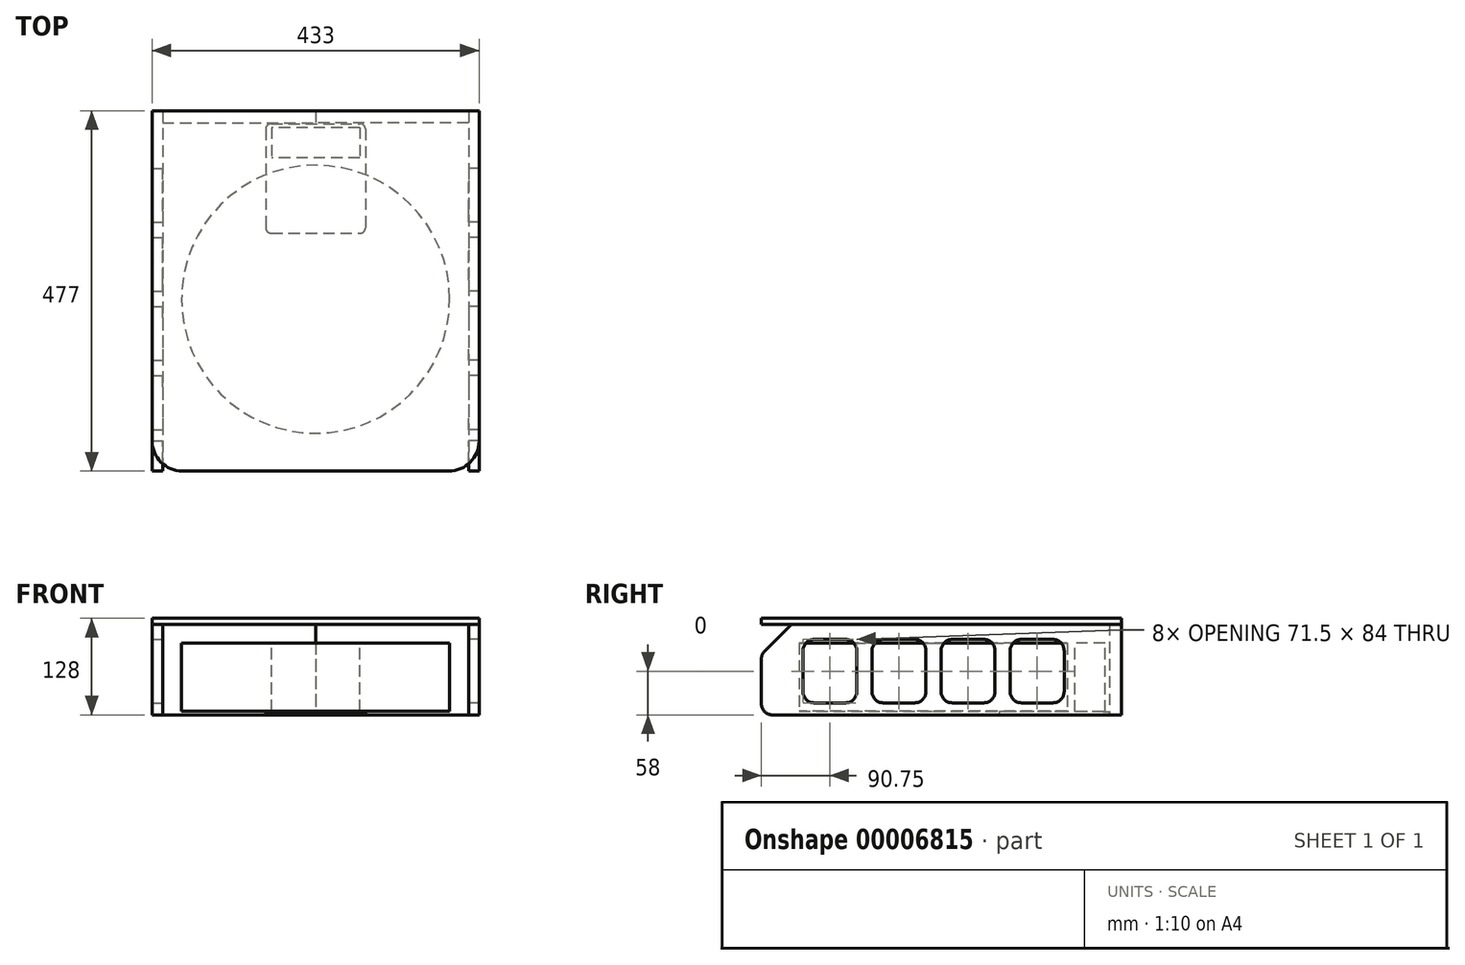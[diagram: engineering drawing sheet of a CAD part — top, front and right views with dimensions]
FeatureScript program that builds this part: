
annotation { "Feature Type Name" : "Feature", "Feature Type Description" : "" }
export const myFeature = defineFeature(function(context is Context, id is Id, definition is map)
    precondition{}
    {
        {
            var Q0;
            Q0=qCreatedBy(makeId("Front.planeOp"),FACE);
            var sketch = newSketch(context, id + "F0", { "sketchPlane" : qUnion([Q0])});
            skLineSegment(sketch, "E0", {"start": v(0, 0) * mm, "end": v(0, 117.94) * mm, "construction": true});
            skPoint(sketch, "E1", {"position": v(0, 5) * mm});
            skPoint(sketch, "E2", {"position": v(0, 95) * mm});
            skSolve(sketch);
        }
        {
            var Q0;
            Q0=qCreatedBy(makeId("Top.planeOp"),FACE);
            var Q1;
            Q1=sQuery(id+"F0.wireOp",VERTEX,"E1");
            cPlane(context, id + "F1", {"entities" : qUnion([Q0, Q1]), "cplaneType" : CPlaneType.PLANE_POINT, "offset" : 25 * mm, "width" : 150 * mm, "height" : 150 * mm});
        }
        {
            var Q0;
            Q0=qCreatedBy(id+"F1.planeOp",FACE);
            var sketch = newSketch(context, id + "F2", { "sketchPlane" : qUnion([Q0])});
            skCircle(sketch, "E3", {"center": v(0, 0) * mm, "radius": 177.5 * mm});
            skSolve(sketch);
        }
        {
            var Q0;
            Q0 = qSketchRegion(id + "F2", true);
            extrude(context, id + "F3", {"entities" : qUnion([Q0]), "depth" : 90 * mm});
        }
        {
            var Q0;
            Q0=qCreatedBy(id+"F1.planeOp",FACE);
            var sketch = newSketch(context, id + "F4", { "sketchPlane" : qUnion([Q0])});
            skLineSegment(sketch, "E4.bottom", {"start": v(-58.5, 227.5) * mm, "end": v(58.5, 227.5) * mm});
            skLineSegment(sketch, "E4.top", {"start": v(-58.5, 187.5) * mm, "end": v(58.5, 187.5) * mm});
            skLineSegment(sketch, "E4.left", {"start": v(-58.5, 187.5) * mm, "end": v(-58.5, 227.5) * mm});
            skLineSegment(sketch, "E4.right", {"start": v(58.5, 187.5) * mm, "end": v(58.5, 227.5) * mm});
            skLineSegment(sketch, "E5", {"start": v(0, 0) * mm, "end": v(0, 187.5) * mm, "construction": true});
            skSolve(sketch);
        }
        {
            var Q0;
            Q0 = qSketchRegion(id + "F4", true);
            var Q1;
            Q1=qCreatedBy(makeId("Top.planeOp"),FACE);
            var Q2;
            Q2=makeQuery(id+"F3.opExtrude","CAP_FACE",FACE,{"disambiguationData":[OSD([sQuery(id+"F2.wireOp",EDGE,"E3")])],"isStart":false});
            extrude(context, id + "F5", {"entities" : qUnion([Q0]), "endBound" : BoundingType.UP_TO_SURFACE, "oppositeDirection" : true, "endBoundEntityFace" : qUnion([Q1]), "depth" : 100 * mm, "hasSecondDirection" : true, "secondDirectionBound" : SecondDirectionBoundingType.UP_TO_SURFACE, "secondDirectionOppositeDirection" : false, "secondDirectionBoundEntityFace" : qUnion([Q2]), "secondDirectionDepth" : 25 * mm});
        }
        {
            var Q0;
            Q0=qCreatedBy(makeId("Top.planeOp"),FACE);
            var sketch = newSketch(context, id + "F6", { "sketchPlane" : qUnion([Q0])});
            skLineSegment(sketch, "E6.bottom", {"start": v(-59, 232.5) * mm, "end": v(59, 232.5) * mm});
            skLineSegment(sketch, "E6.top", {"start": v(-59, 87.5) * mm, "end": v(59, 87.5) * mm});
            skLineSegment(sketch, "E6.left", {"start": v(-66, 225.5) * mm, "end": v(-66, 94.5) * mm});
            skLineSegment(sketch, "E6.right", {"start": v(66, 225.5) * mm, "end": v(66, 94.5) * mm});
            skPoint(sketch, "E7.visualSharp", {"position": v(-66, 232.5) * mm});
            skArc(sketch, "E7.filletArc", {"start": v(-59, 232.5) * mm, "mid": v(-63.95, 230.45) * mm, "end": v(-66, 225.5) * mm});
            skPoint(sketch, "E8.visualSharp", {"position": v(66, 232.5) * mm});
            skArc(sketch, "E8.filletArc", {"start": v(66, 225.5) * mm, "mid": v(63.95, 230.45) * mm, "end": v(59, 232.5) * mm});
            skPoint(sketch, "E9.visualSharp", {"position": v(66, 87.5) * mm});
            skArc(sketch, "E9.filletArc", {"start": v(59, 87.5) * mm, "mid": v(63.95, 89.55) * mm, "end": v(66, 94.5) * mm});
            skPoint(sketch, "E10.visualSharp", {"position": v(-66, 87.5) * mm});
            skArc(sketch, "E10.filletArc", {"start": v(-66, 94.5) * mm, "mid": v(-63.95, 89.55) * mm, "end": v(-59, 87.5) * mm});
            skLineSegment(sketch, "E11", {"start": v(0, 0) * mm, "end": v(0, 87.5) * mm, "construction": true});
            skSolve(sketch);
        }
        {
            var Q0;
            Q0 = qSketchRegion(id + "F6", true);
            extrude(context, id + "F7", {"entities" : qUnion([Q0]), "operationType" : NewBodyOperationType.ADD, "depth" : 4.5 * mm});
        }
        {
            var Q0;
            Q0=makeQuery(id+"F2.imprint","IMPRINT",FACE,{"disambiguationData":[TD([[makeQuery(id+"F2.imprint","IMPRINT",EDGE,{"derivedFrom":sQuery(id+"F2.wireOp",EDGE,"E3")}),1.0]])]});
            var sketch = newSketch(context, id + "F8", { "sketchPlane" : qUnion([Q0])});
            skLineSegment(sketch, "E12", {"start": v(0, -177.5) * mm, "end": v(0, 233.5) * mm, "construction": true});
            skLineSegment(sketch, "E13", {"start": v(-177.5, 233.5) * mm, "end": v(0, 233.5) * mm, "construction": true});
            skLineSegment(sketch, "E14", {"start": v(-177.5, 233.5) * mm, "end": v(-177.5, -177.5) * mm, "construction": true});
            skLineSegment(sketch, "E15", {"start": v(0, -177.5) * mm, "end": v(-177.5, -177.5) * mm, "construction": true});
            skSolve(sketch);
        }
        {
            var Q0;
            Q0=qCreatedBy(makeId("Front.planeOp"),FACE);
            var Q1;
            Q1=sQuery(id+"F8.wireOp",VERTEX,"E12.end");
            cPlane(context, id + "F9", {"entities" : qUnion([Q0, Q1]), "cplaneType" : CPlaneType.PLANE_POINT, "offset" : 25 * mm, "width" : 150 * mm, "height" : 150 * mm});
        }
        {
            var Q0;
            Q0=qCreatedBy(id+"F9.planeOp",FACE);
            var sketch = newSketch(context, id + "F10", { "sketchPlane" : qUnion([Q0])});
            skLineSegment(sketch, "E16.bottom", {"start": v(-202.5, 120) * mm, "end": v(0, 120) * mm});
            skLineSegment(sketch, "E16.top", {"start": v(-202.5, 0) * mm, "end": v(0, 0) * mm});
            skLineSegment(sketch, "E16.left", {"start": v(-202.5, 120) * mm, "end": v(-202.5, 0) * mm});
            skLineSegment(sketch, "E16.right", {"start": v(0, 120) * mm, "end": v(0, 0) * mm});
            skLineSegment(sketch, "E17", {"start": v(-156.5, 114) * mm, "end": v(-200.5, 114) * mm, "construction": true});
            skLineSegment(sketch, "E18", {"start": v(-200.5, 114) * mm, "end": v(-200.5, 76.5) * mm, "construction": true});
            skLineSegment(sketch, "E19", {"start": v(-156.5, 76.5) * mm, "end": v(-156.5, 114) * mm, "construction": true});
            skLineSegment(sketch, "E20", {"start": v(-156.5, 76.5) * mm, "end": v(-200.5, 76.5) * mm, "construction": true});
            skLineSegment(sketch, "E21", {"start": v(-156.5, 90) * mm, "end": v(-162.5, 90) * mm, "construction": true});
            skLineSegment(sketch, "E22", {"start": v(-162.5, 90) * mm, "end": v(-194.5, 90) * mm, "construction": true});
            skLineSegment(sketch, "E23", {"start": v(-194.5, 90) * mm, "end": v(-200.5, 90) * mm, "construction": true});
            skLineSegment(sketch, "E24", {"start": v(-156.5, 108) * mm, "end": v(-162.5, 108) * mm, "construction": true});
            skLineSegment(sketch, "E25", {"start": v(-162.5, 108) * mm, "end": v(-194.5, 108) * mm, "construction": true});
            skLineSegment(sketch, "E26", {"start": v(-194.5, 108) * mm, "end": v(-200.5, 108) * mm, "construction": true});
            skCircle(sketch, "E27", {"center": v(-162.5, 108) * mm, "radius": 2 * mm, "construction": true});
            skCircle(sketch, "E28", {"center": v(-194.5, 108) * mm, "radius": 2 * mm, "construction": true});
            skCircle(sketch, "E29", {"center": v(-194.5, 90) * mm, "radius": 2 * mm, "construction": true});
            skCircle(sketch, "E30", {"center": v(-162.5, 90) * mm, "radius": 2 * mm, "construction": true});
            skLineSegment(sketch, "E31", {"start": v(-162.5, 90) * mm, "end": v(-194.5, 108) * mm, "construction": true});
            skLineSegment(sketch, "E32", {"start": v(-162.5, 108) * mm, "end": v(-194.5, 90) * mm, "construction": true});
            skPoint(sketch, "E33", {"position": v(-178.5, 99) * mm});
            skSolve(sketch);
        }
        {
            var Q0;
            Q0 = qSketchRegion(id + "F10", true);
            extrude(context, id + "F11", {"entities" : qUnion([Q0]), "oppositeDirection" : true, "depth" : 16 * mm});
        }
        {
            var Q0;
            Q0=qCreatedBy(makeId("Front.planeOp"),FACE);
            var Q1;
            Q1=sQuery(id+"F8.wireOp",VERTEX,"E15.start");
            cPlane(context, id + "F12", {"entities" : qUnion([Q0, Q1]), "cplaneType" : CPlaneType.PLANE_POINT, "offset" : 25 * mm, "width" : 150 * mm, "height" : 150 * mm});
        }
        {
            var Q0;
            Q0=makeQuery(id+"F11.opExtrude","SWEPT_FACE",FACE,{"disambiguationData":[OSD([sQuery(id+"F10.wireOp",EDGE,"E16.left")])]});
            var sketch = newSketch(context, id + "F13", { "sketchPlane" : qUnion([Q0])});
            skLineSegment(sketch, "E34", {"start": v(-249.5, 120) * mm, "end": v(-249.5, 0) * mm});
            skLineSegment(sketch, "E35", {"start": v(227.5, 0) * mm, "end": v(-249.5, 0) * mm});
            skLineSegment(sketch, "E36", {"start": v(227.5, 0) * mm, "end": v(227.5, 80) * mm});
            skLineSegment(sketch, "E37", {"start": v(227.5, 80) * mm, "end": v(187.5, 120) * mm});
            skLineSegment(sketch, "E38", {"start": v(-249.5, 120) * mm, "end": v(187.5, 120) * mm});
            skLineSegment(sketch, "E39.bottom", {"start": v(-102, 100) * mm, "end": v(-173.5, 100) * mm});
            skLineSegment(sketch, "E39.top", {"start": v(-102, 16) * mm, "end": v(-173.5, 16) * mm});
            skLineSegment(sketch, "E39.left", {"start": v(-173.5, 100) * mm, "end": v(-173.5, 16) * mm});
            skLineSegment(sketch, "E39.right", {"start": v(-102, 100) * mm, "end": v(-102, 16) * mm});
            skLineSegment(sketch, "E40.bottom", {"start": v(-10.5, 100) * mm, "end": v(-82, 100) * mm});
            skLineSegment(sketch, "E40.left", {"start": v(-82, 100) * mm, "end": v(-82, 16) * mm});
            skLineSegment(sketch, "E41.top", {"start": v(-10.5, 16) * mm, "end": v(-82, 16) * mm});
            skLineSegment(sketch, "E41.left", {"start": v(-10.5, 100) * mm, "end": v(-10.5, 16) * mm});
            skLineSegment(sketch, "E42.bottom", {"start": v(101, 100) * mm, "end": v(172.5, 100) * mm});
            skLineSegment(sketch, "E42.top", {"start": v(101, 16) * mm, "end": v(172.5, 16) * mm});
            skLineSegment(sketch, "E42.left", {"start": v(101, 100) * mm, "end": v(101, 16) * mm});
            skLineSegment(sketch, "E42.right", {"start": v(172.5, 100) * mm, "end": v(172.5, 16) * mm});
            skLineSegment(sketch, "E43", {"start": v(227.5, 80) * mm, "end": v(227.5, 120) * mm, "construction": true});
            skLineSegment(sketch, "E44.bottom", {"start": v(9.5, 100) * mm, "end": v(81, 100) * mm});
            skLineSegment(sketch, "E44.top", {"start": v(9.5, 16) * mm, "end": v(81, 16) * mm});
            skLineSegment(sketch, "E44.left", {"start": v(81, 100) * mm, "end": v(81, 16) * mm});
            skLineSegment(sketch, "E44.right", {"start": v(9.5, 100) * mm, "end": v(9.5, 16) * mm});
            skPoint(sketch, "E45", {"position": v(101, 120) * mm});
            skLineSegment(sketch, "E46", {"start": v(187.5, 120) * mm, "end": v(187.5, 0) * mm, "construction": true});
            skLineSegment(sketch, "E47", {"start": v(-102, 16) * mm, "end": v(-82, 16) * mm, "construction": true});
            skLineSegment(sketch, "E48", {"start": v(9.5, 16) * mm, "end": v(-10.5, 16) * mm, "construction": true});
            skLineSegment(sketch, "E49", {"start": v(81, 16) * mm, "end": v(101, 16) * mm, "construction": true});
            skPoint(sketch, "E50", {"position": v(177.5, 23.11) * mm});
            skSolve(sketch);
        }
        {
            var Q0;
            Q0 = qSketchRegion(id + "F13", true);
            extrude(context, id + "F14", {"entities" : qUnion([Q0]), "depth" : 14 * mm});
        }
        {
            var Q0;
            Q0=makeQuery(id+"F14.opExtrude","SWEPT_FACE",FACE,{"disambiguationData":[OSD([sQuery(id+"F13.wireOp",EDGE,"E38")])]});
            var sketch = newSketch(context, id + "F15", { "sketchPlane" : qUnion([Q0])});
            skLineSegment(sketch, "E51", {"start": v(-216.5, -144.25) * mm, "end": v(-202.5, -144.25) * mm, "construction": true});
            skCircle(sketch, "E52", {"center": v(-209.5, -144.25) * mm, "radius": 5.05 * mm});
            skSolve(sketch);
        }
        {
            var Q0;
            Q0=makeQuery(id+"F14.opExtrude","SWEPT_EDGE",EDGE,{"disambiguationData":[OSD([sQuery(id+"F13.wireOp",EDGE,"E40.bottom"),sQuery(id+"F13.wireOp",EDGE,"E40.left")])]});
            var Q1;
            Q1=makeQuery(id+"F14.opExtrude","SWEPT_EDGE",EDGE,{"disambiguationData":[OSD([sQuery(id+"F13.wireOp",EDGE,"E39.bottom"),sQuery(id+"F13.wireOp",EDGE,"E39.left")])]});
            var Q2;
            Q2=makeQuery(id+"F14.opExtrude","SWEPT_EDGE",EDGE,{"disambiguationData":[OSD([sQuery(id+"F13.wireOp",EDGE,"E41.bottom"),sQuery(id+"F13.wireOp",EDGE,"E41.left")])]});
            var Q3;
            Q3=makeQuery(id+"F14.opExtrude","SWEPT_EDGE",EDGE,{"disambiguationData":[OSD([sQuery(id+"F13.wireOp",EDGE,"E35"),sQuery(id+"F13.wireOp",EDGE,"E36")])]});
            var Q4;
            Q4=makeQuery(id+"F14.opExtrude","SWEPT_EDGE",EDGE,{"disambiguationData":[OSD([sQuery(id+"F13.wireOp",EDGE,"E36"),sQuery(id+"F13.wireOp",EDGE,"E37")])]});
            var Q5;
            Q5=makeQuery(id+"F14.opExtrude","SWEPT_EDGE",EDGE,{"disambiguationData":[OSD([sQuery(id+"F13.wireOp",EDGE,"E39.top"),sQuery(id+"F13.wireOp",EDGE,"E39.left")])]});
            var Q6;
            Q6=makeQuery(id+"F14.opExtrude","SWEPT_EDGE",EDGE,{"disambiguationData":[OSD([sQuery(id+"F13.wireOp",EDGE,"E40.top"),sQuery(id+"F13.wireOp",EDGE,"E40.left")])]});
            var Q7;
            Q7=makeQuery(id+"F14.opExtrude","SWEPT_EDGE",EDGE,{"disambiguationData":[OSD([sQuery(id+"F13.wireOp",EDGE,"E41.top"),sQuery(id+"F13.wireOp",EDGE,"E41.left")])]});
            var Q8;
            Q8=makeQuery(id+"F14.opExtrude","SWEPT_EDGE",EDGE,{"disambiguationData":[OSD([sQuery(id+"F13.wireOp",EDGE,"E41.top"),sQuery(id+"F13.wireOp",EDGE,"E41.right")])]});
            var Q9;
            Q9=makeQuery(id+"F14.opExtrude","SWEPT_EDGE",EDGE,{"disambiguationData":[OSD([sQuery(id+"F13.wireOp",EDGE,"E40.top"),sQuery(id+"F13.wireOp",EDGE,"E40.right")])]});
            var Q10;
            Q10=makeQuery(id+"F14.opExtrude","SWEPT_EDGE",EDGE,{"disambiguationData":[OSD([sQuery(id+"F13.wireOp",EDGE,"E39.top"),sQuery(id+"F13.wireOp",EDGE,"E39.right")])]});
            var Q11;
            Q11=makeQuery(id+"F14.opExtrude","SWEPT_EDGE",EDGE,{"disambiguationData":[OSD([sQuery(id+"F13.wireOp",EDGE,"E41.bottom"),sQuery(id+"F13.wireOp",EDGE,"E41.right")])]});
            var Q12;
            Q12=makeQuery(id+"F14.opExtrude","SWEPT_EDGE",EDGE,{"disambiguationData":[OSD([sQuery(id+"F13.wireOp",EDGE,"E40.bottom"),sQuery(id+"F13.wireOp",EDGE,"E40.right")])]});
            var Q13;
            Q13=makeQuery(id+"F14.opExtrude","SWEPT_EDGE",EDGE,{"disambiguationData":[OSD([sQuery(id+"F13.wireOp",EDGE,"E39.bottom"),sQuery(id+"F13.wireOp",EDGE,"E39.right")])]});
            var Q14;
            Q14=makeQuery(id+"F14.opExtrude","SWEPT_EDGE",EDGE,{"disambiguationData":[OSD([sQuery(id+"F13.wireOp",EDGE,"E42.top"),sQuery(id+"F13.wireOp",EDGE,"E42.left")])]});
            var Q15;
            Q15=makeQuery(id+"F14.opExtrude","SWEPT_EDGE",EDGE,{"disambiguationData":[OSD([sQuery(id+"F13.wireOp",EDGE,"E42.top"),sQuery(id+"F13.wireOp",EDGE,"E42.right")])]});
            var Q16;
            Q16=makeQuery(id+"F14.opExtrude","SWEPT_EDGE",EDGE,{"disambiguationData":[OSD([sQuery(id+"F13.wireOp",EDGE,"E42.bottom"),sQuery(id+"F13.wireOp",EDGE,"E42.right")])]});
            var Q17;
            Q17=makeQuery(id+"F14.opExtrude","SWEPT_EDGE",EDGE,{"disambiguationData":[OSD([sQuery(id+"F13.wireOp",EDGE,"E42.bottom"),sQuery(id+"F13.wireOp",EDGE,"E42.left")])]});
            var Q18;
            Q18=makeQuery(id+"F11.opExtrude","SWEPT_EDGE",EDGE,{"disambiguationData":[OSD([sQuery(id+"F10.wireOp",EDGE,"42908f74-1b4f-4dd7-a1f5-b5feeaa3a12f.bottom"),sQuery(id+"F10.wireOp",EDGE,"42908f74-1b4f-4dd7-a1f5-b5feeaa3a12f.right")])]});
            var Q19;
            Q19=makeQuery(id+"F11.opExtrude","SWEPT_EDGE",EDGE,{"disambiguationData":[OSD([sQuery(id+"F10.wireOp",EDGE,"7d3d7e17-e7ec-4853-b92f-0c4755d0859e.bottom"),sQuery(id+"F10.wireOp",EDGE,"7d3d7e17-e7ec-4853-b92f-0c4755d0859e.right")])]});
            var Q20;
            Q20=makeQuery(id+"F11.opExtrude","SWEPT_EDGE",EDGE,{"disambiguationData":[OSD([sQuery(id+"F10.wireOp",EDGE,"7d3d7e17-e7ec-4853-b92f-0c4755d0859e.top"),sQuery(id+"F10.wireOp",EDGE,"7d3d7e17-e7ec-4853-b92f-0c4755d0859e.right")])]});
            var Q21;
            Q21=makeQuery(id+"F11.opExtrude","SWEPT_EDGE",EDGE,{"disambiguationData":[OSD([sQuery(id+"F10.wireOp",EDGE,"42908f74-1b4f-4dd7-a1f5-b5feeaa3a12f.top"),sQuery(id+"F10.wireOp",EDGE,"42908f74-1b4f-4dd7-a1f5-b5feeaa3a12f.right")])]});
            var Q22;
            Q22=makeQuery(id+"F11.opExtrude","SWEPT_EDGE",EDGE,{"disambiguationData":[OSD([sQuery(id+"F10.wireOp",EDGE,"7d3d7e17-e7ec-4853-b92f-0c4755d0859e.bottom"),sQuery(id+"F10.wireOp",EDGE,"7d3d7e17-e7ec-4853-b92f-0c4755d0859e.left")])]});
            var Q23;
            Q23=makeQuery(id+"F11.opExtrude","SWEPT_EDGE",EDGE,{"disambiguationData":[OSD([sQuery(id+"F10.wireOp",EDGE,"42908f74-1b4f-4dd7-a1f5-b5feeaa3a12f.bottom"),sQuery(id+"F10.wireOp",EDGE,"42908f74-1b4f-4dd7-a1f5-b5feeaa3a12f.left")])]});
            var Q24;
            Q24=makeQuery(id+"F11.opExtrude","SWEPT_EDGE",EDGE,{"disambiguationData":[OSD([sQuery(id+"F10.wireOp",EDGE,"42908f74-1b4f-4dd7-a1f5-b5feeaa3a12f.top"),sQuery(id+"F10.wireOp",EDGE,"42908f74-1b4f-4dd7-a1f5-b5feeaa3a12f.left")])]});
            var Q25;
            Q25=makeQuery(id+"F11.opExtrude","SWEPT_EDGE",EDGE,{"disambiguationData":[OSD([sQuery(id+"F10.wireOp",EDGE,"7d3d7e17-e7ec-4853-b92f-0c4755d0859e.top"),sQuery(id+"F10.wireOp",EDGE,"7d3d7e17-e7ec-4853-b92f-0c4755d0859e.left")])]});
            var Q26;
            Q26=makeQuery(id+"F14.opExtrude","SWEPT_EDGE",EDGE,{"disambiguationData":[OSD([sQuery(id+"F13.wireOp",EDGE,"E44.top"),sQuery(id+"F13.wireOp",EDGE,"E44.right")])]});
            var Q27;
            Q27=makeQuery(id+"F14.opExtrude","SWEPT_EDGE",EDGE,{"disambiguationData":[OSD([sQuery(id+"F13.wireOp",EDGE,"E44.bottom"),sQuery(id+"F13.wireOp",EDGE,"E44.right")])]});
            var Q28;
            Q28=makeQuery(id+"F14.opExtrude","SWEPT_EDGE",EDGE,{"disambiguationData":[OSD([sQuery(id+"F13.wireOp",EDGE,"E44.top"),sQuery(id+"F13.wireOp",EDGE,"E44.left")])]});
            var Q29;
            Q29=makeQuery(id+"F14.opExtrude","SWEPT_EDGE",EDGE,{"disambiguationData":[OSD([sQuery(id+"F13.wireOp",EDGE,"E44.bottom"),sQuery(id+"F13.wireOp",EDGE,"E44.left")])]});
            fillet(context, id + "F16", {"entities" : qUnion([Q0, Q1, Q2, Q3, Q4, Q5, Q6, Q7, Q8, Q9, Q10, Q11, Q12, Q13, Q14, Q15, Q16, Q17, Q18, Q19, Q20, Q21, Q22, Q23, Q24, Q25, Q26, Q27, Q28, Q29]), "radius" : 15 * mm, "tangentPropagation" : true, "allowEdgeOverflow" : false});
        }
        {
            var Q0;
            Q0=makeQuery(id+"F11.opExtrude","SWEPT_BODY",BODY,{"disambiguationData":[OSD([sQuery(id+"F10.wireOp",EDGE,"E16.bottom"),sQuery(id+"F10.wireOp",EDGE,"E16.top"),sQuery(id+"F10.wireOp",EDGE,"E16.left"),sQuery(id+"F10.wireOp",EDGE,"E16.right"),sQuery(id+"F10.wireOp",EDGE,"5cda8c20-23ce-490b-b1d3-2776b074a77f"),sQuery(id+"F10.wireOp",EDGE,"887f5a22-7d88-485e-85bc-e6de6f7dc943"),sQuery(id+"F10.wireOp",EDGE,"7d3d7e17-e7ec-4853-b92f-0c4755d0859e.bottom"),sQuery(id+"F10.wireOp",EDGE,"7d3d7e17-e7ec-4853-b92f-0c4755d0859e.top"),sQuery(id+"F10.wireOp",EDGE,"7d3d7e17-e7ec-4853-b92f-0c4755d0859e.left"),sQuery(id+"F10.wireOp",EDGE,"7d3d7e17-e7ec-4853-b92f-0c4755d0859e.right")])]});
            var Q1;
            Q1=qCreatedBy(makeId("Right.planeOp"),FACE);
            mirror(context, id + "F17", {"entities" : qUnion([Q0]), "mirrorPlane" : qUnion([Q1])});
        }
        {
            var Q0;
            Q0=makeQuery(id+"F14.opExtrude","SWEPT_BODY",BODY,{"disambiguationData":[OSD([sQuery(id+"F13.wireOp",EDGE,"E34"),sQuery(id+"F13.wireOp",EDGE,"E35"),sQuery(id+"F13.wireOp",EDGE,"E36"),sQuery(id+"F13.wireOp",EDGE,"E37"),sQuery(id+"F13.wireOp",EDGE,"E38"),sQuery(id+"F13.wireOp",EDGE,"E39.bottom"),sQuery(id+"F13.wireOp",EDGE,"E39.top"),sQuery(id+"F13.wireOp",EDGE,"E39.left"),sQuery(id+"F13.wireOp",EDGE,"E39.right"),sQuery(id+"F13.wireOp",EDGE,"E40.bottom"),sQuery(id+"F13.wireOp",EDGE,"E40.left"),sQuery(id+"F13.wireOp",EDGE,"E41.top"),sQuery(id+"F13.wireOp",EDGE,"E41.left"),sQuery(id+"F13.wireOp",EDGE,"E42.bottom"),sQuery(id+"F13.wireOp",EDGE,"E42.top"),sQuery(id+"F13.wireOp",EDGE,"E42.left"),sQuery(id+"F13.wireOp",EDGE,"E42.right")])]});
            var Q1;
            Q1=qCreatedBy(makeId("Right.planeOp"),FACE);
            mirror(context, id + "F18", {"entities" : qUnion([Q0]), "mirrorPlane" : qUnion([Q1])});
        }
        {
            var Q0;
            Q0=qCreatedBy(makeId("Top.planeOp"),FACE);
            var Q1;
            Q1=makeQuery(id+"F17.opPattern","COPY",VERTEX,{"derivedFrom":makeQuery(id+"F11.opExtrude","CAP_VERTEX",VERTEX,{"disambiguationData":[OSD([sQuery(id+"F10.wireOp",EDGE,"E16.bottom"),sQuery(id+"F10.wireOp",EDGE,"E16.right")])],"isStart":true}),"instanceName":"1"});
            cPlane(context, id + "F19", {"entities" : qUnion([Q0, Q1]), "cplaneType" : CPlaneType.PLANE_POINT, "offset" : 150 * mm, "width" : 150 * mm, "height" : 150 * mm});
        }
        {
            var Q0;
            Q0=qCreatedBy(id+"F19.planeOp",FACE);
            var sketch = newSketch(context, id + "F20", { "sketchPlane" : qUnion([Q0])});
            skLineSegment(sketch, "E53.bottom", {"start": v(216.5, 249.5) * mm, "end": v(-216.5, 249.5) * mm});
            skLineSegment(sketch, "E53.top", {"start": v(176.5, -227.5) * mm, "end": v(-176.5, -227.5) * mm});
            skLineSegment(sketch, "E53.left", {"start": v(-216.5, 249.5) * mm, "end": v(-216.5, -187.5) * mm});
            skLineSegment(sketch, "E53.right", {"start": v(216.5, 249.5) * mm, "end": v(216.5, -187.5) * mm});
            skCircle(sketch, "E54", {"center": v(0, 0) * mm, "radius": 187.5 * mm, "construction": true});
            skLineSegment(sketch, "E55", {"start": v(-216.5, -187.5) * mm, "end": v(216.5, -187.5) * mm, "construction": true});
            skArc(sketch, "E56", {"start": v(-216.5, -187.5) * mm, "mid": v(-204.78, -215.78) * mm, "end": v(-176.5, -227.5) * mm});
            skArc(sketch, "E57", {"start": v(176.5, -227.5) * mm, "mid": v(204.78, -215.78) * mm, "end": v(216.5, -187.5) * mm});
            skSolve(sketch);
        }
        {
            var Q0;
            Q0 = qSketchRegion(id + "F20", true);
            extrude(context, id + "F21", {"entities" : qUnion([Q0]), "depth" : 8 * mm});
        }
    });
